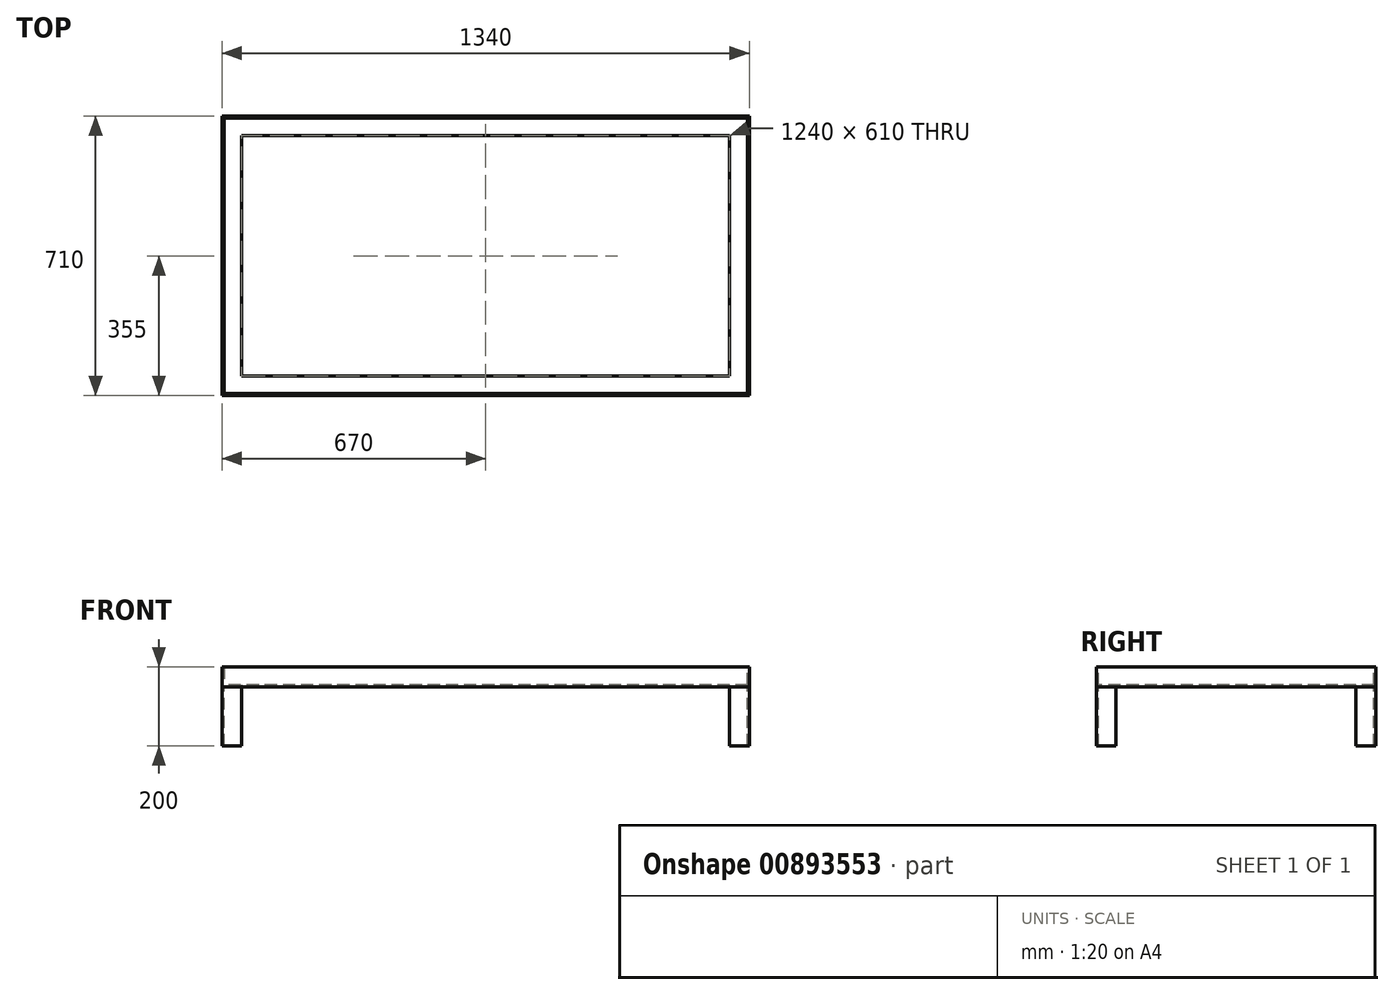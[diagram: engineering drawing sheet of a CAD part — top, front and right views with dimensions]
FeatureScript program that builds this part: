
annotation { "Feature Type Name" : "Feature", "Feature Type Description" : "" }
export const myFeature = defineFeature(function(context is Context, id is Id, definition is map)
    precondition{}
    {
        {
            var Q0;
            Q0=qCreatedBy(makeId("Right.planeOp"),FACE);
            var sketch = newSketch(context, id + "F0", { "sketchPlane" : qUnion([Q0])});
            skLineSegment(sketch, "E0.bottom", {"start": v(0, 0) * mm, "end": v(-50, 0) * mm});
            skLineSegment(sketch, "E0.top", {"start": v(-5, 5) * mm, "end": v(-50, 5) * mm});
            skLineSegment(sketch, "E0.left", {"start": v(0, 0) * mm, "end": v(0, 5) * mm});
            skLineSegment(sketch, "E0.right", {"start": v(-50, 0) * mm, "end": v(-50, 5) * mm});
            skLineSegment(sketch, "E1.bottom", {"start": v(0, 0) * mm, "end": v(-5, 0) * mm});
            skLineSegment(sketch, "E1.top", {"start": v(0, 50) * mm, "end": v(-5, 50) * mm});
            skLineSegment(sketch, "E1.left", {"start": v(0, 0) * mm, "end": v(0, 50) * mm});
            skLineSegment(sketch, "E1.right", {"start": v(-5, 5) * mm, "end": v(-5, 50) * mm});
            skSolve(sketch);
        }
        {
            var Q0;
            Q0 = qSketchRegion(id + "F0", true);
            extrude(context, id + "F1", {"entities" : qUnion([Q0]), "endBound" : BoundingType.SYMMETRIC, "depth" : 1340 * mm, "offsetDistance" : 25 * mm});
        }
        {
            var Q0;
            Q0=makeQuery(id+"F1.opExtrude","SWEPT_FACE",FACE,{"disambiguationData":[OSD([sQuery(id+"F0.wireOp",EDGE,"E1.left")])]});
            var sketch = newSketch(context, id + "F2", { "sketchPlane" : qUnion([Q0])});
            skLineSegment(sketch, "E2", {"start": v(670, 0) * mm, "end": v(620, 0) * mm});
            skLineSegment(sketch, "E3", {"start": v(620, 0) * mm, "end": v(620, 5) * mm});
            skLineSegment(sketch, "E4", {"start": v(620, 5) * mm, "end": v(665, 5) * mm});
            skLineSegment(sketch, "E5", {"start": v(665, 5) * mm, "end": v(665, 50) * mm});
            skLineSegment(sketch, "E6", {"start": v(665, 50) * mm, "end": v(670, 50) * mm});
            skLineSegment(sketch, "E7", {"start": v(670, 50) * mm, "end": v(670, 0) * mm});
            skSolve(sketch);
        }
        {
            var Q0;
            Q0 = qSketchRegion(id + "F2", true);
            extrude(context, id + "F3", {"entities" : qUnion([Q0]), "operationType" : NewBodyOperationType.ADD, "oppositeDirection" : true, "depth" : 710 * mm, "offsetDistance" : 25 * mm});
        }
        {
            var Q0;
            Q0=makeQuery(id+"F3.boolean.opBoolean","MERGE",FACE,{"derivedFrom":[makeQuery(id+"F1.opExtrude","CAP_FACE",FACE,{"disambiguationData":[OSD([sQuery(id+"F0.wireOp",EDGE,"E0.bottom"),sQuery(id+"F0.wireOp",EDGE,"E0.top"),sQuery(id+"F0.wireOp",EDGE,"E0.right"),sQuery(id+"F0.wireOp",EDGE,"E1.bottom"),sQuery(id+"F0.wireOp",EDGE,"E1.top"),sQuery(id+"F0.wireOp",EDGE,"E1.left"),sQuery(id+"F0.wireOp",EDGE,"E1.right")])],"isStart":true}),makeQuery(id+"F3.opExtrude","SWEPT_FACE",FACE,{"disambiguationData":[OSD([sQuery(id+"F2.wireOp",EDGE,"E7")])]})]});
            var sketch = newSketch(context, id + "F4", { "sketchPlane" : qUnion([Q0])});
            skLineSegment(sketch, "E8", {"start": v(710, 50) * mm, "end": v(710, 0) * mm});
            skLineSegment(sketch, "E9", {"start": v(710, 0) * mm, "end": v(660, 0) * mm});
            skLineSegment(sketch, "E10", {"start": v(660, 0) * mm, "end": v(660, 5) * mm});
            skLineSegment(sketch, "E11", {"start": v(660, 5) * mm, "end": v(705, 5) * mm});
            skLineSegment(sketch, "E12", {"start": v(705, 5) * mm, "end": v(705, 50) * mm});
            skLineSegment(sketch, "E13", {"start": v(705, 50) * mm, "end": v(710, 50) * mm});
            skSolve(sketch);
        }
        {
            var Q0;
            Q0 = qSketchRegion(id + "F4", true);
            extrude(context, id + "F5", {"entities" : qUnion([Q0]), "operationType" : NewBodyOperationType.ADD, "oppositeDirection" : true, "depth" : 1340 * mm, "offsetDistance" : 25 * mm});
        }
        {
            var Q0;
            Q0=makeQuery(id+"F5.boolean.opBoolean","MERGE",FACE,{"derivedFrom":[makeQuery(id+"F3.opExtrude","CAP_FACE",FACE,{"disambiguationData":[OSD([sQuery(id+"F2.wireOp",EDGE,"E2"),sQuery(id+"F2.wireOp",EDGE,"E3"),sQuery(id+"F2.wireOp",EDGE,"E4"),sQuery(id+"F2.wireOp",EDGE,"E5"),sQuery(id+"F2.wireOp",EDGE,"E6"),sQuery(id+"F2.wireOp",EDGE,"E7")])],"isStart":false}),makeQuery(id+"F5.opExtrude","SWEPT_FACE",FACE,{"disambiguationData":[OSD([sQuery(id+"F4.wireOp",EDGE,"E8")])]})]});
            var sketch = newSketch(context, id + "F6", { "sketchPlane" : qUnion([Q0])});
            skLineSegment(sketch, "E14", {"start": v(670, 50) * mm, "end": v(670, 0) * mm});
            skLineSegment(sketch, "E15", {"start": v(670, 0) * mm, "end": v(620, 0) * mm});
            skLineSegment(sketch, "E16", {"start": v(620, 0) * mm, "end": v(620, 5) * mm});
            skLineSegment(sketch, "E17", {"start": v(620, 5) * mm, "end": v(665, 5) * mm});
            skLineSegment(sketch, "E18", {"start": v(665, 5) * mm, "end": v(665, 50) * mm});
            skLineSegment(sketch, "E19", {"start": v(665, 50) * mm, "end": v(670, 50) * mm});
            skSolve(sketch);
        }
        {
            var Q0;
            Q0 = qSketchRegion(id + "F6", true);
            extrude(context, id + "F7", {"entities" : qUnion([Q0]), "operationType" : NewBodyOperationType.ADD, "oppositeDirection" : true, "depth" : 710 * mm, "offsetDistance" : 25 * mm});
        }
        {
            var Q0;
            Q0=makeQuery(id+"F7.boolean.opBoolean","MERGE",FACE,{"derivedFrom":[makeQuery(id+"F5.boolean.opBoolean","MERGE",FACE,{"derivedFrom":[makeQuery(id+"F3.boolean.opBoolean","MERGE",FACE,{"derivedFrom":[makeQuery(id+"F1.opExtrude","SWEPT_FACE",FACE,{"disambiguationData":[OSD([sQuery(id+"F0.wireOp",EDGE,"E0.bottom"),sQuery(id+"F0.wireOp",EDGE,"E1.bottom")])]}),makeQuery(id+"F3.opExtrude","SWEPT_FACE",FACE,{"disambiguationData":[OSD([sQuery(id+"F2.wireOp",EDGE,"E2")])]})]}),makeQuery(id+"F5.opExtrude","SWEPT_FACE",FACE,{"disambiguationData":[OSD([sQuery(id+"F4.wireOp",EDGE,"E9")])]})]}),makeQuery(id+"F7.opExtrude","SWEPT_FACE",FACE,{"disambiguationData":[OSD([sQuery(id+"F6.wireOp",EDGE,"E15")])]})]});
            var sketch = newSketch(context, id + "F8", { "sketchPlane" : qUnion([Q0])});
            skLineSegment(sketch, "E20", {"start": v(-670, 0) * mm, "end": v(-670, 50) * mm});
            skLineSegment(sketch, "E21", {"start": v(-670, 50) * mm, "end": v(-665, 50) * mm});
            skLineSegment(sketch, "E22", {"start": v(-665, 50) * mm, "end": v(-665, 5) * mm});
            skLineSegment(sketch, "E23", {"start": v(-665, 5) * mm, "end": v(-620, 5) * mm});
            skLineSegment(sketch, "E24", {"start": v(-620, 5) * mm, "end": v(-620, 0) * mm});
            skLineSegment(sketch, "E25", {"start": v(-620, 0) * mm, "end": v(-670, 0) * mm});
            skLineSegment(sketch, "E26", {"start": v(-670, 710) * mm, "end": v(-670, 660) * mm});
            skLineSegment(sketch, "E27", {"start": v(-670, 660) * mm, "end": v(-665, 660) * mm});
            skLineSegment(sketch, "E28", {"start": v(-665, 660) * mm, "end": v(-665, 705) * mm});
            skLineSegment(sketch, "E29", {"start": v(-665, 705) * mm, "end": v(-620, 705) * mm});
            skLineSegment(sketch, "E30", {"start": v(-620, 705) * mm, "end": v(-620, 710) * mm});
            skLineSegment(sketch, "E31", {"start": v(-620, 710) * mm, "end": v(-670, 710) * mm});
            skLineSegment(sketch, "E32.MirrorCS", {"start": v(620, 0) * mm, "end": v(670, 0) * mm});
            skLineSegment(sketch, "E33.MirrorCS", {"start": v(665, 5) * mm, "end": v(620, 5) * mm});
            skLineSegment(sketch, "E34.MirrorCS", {"start": v(620, 5) * mm, "end": v(620, 0) * mm});
            skLineSegment(sketch, "E35.MirrorCS", {"start": v(670, 50) * mm, "end": v(665, 50) * mm});
            skLineSegment(sketch, "E36.MirrorCS", {"start": v(665, 50) * mm, "end": v(665, 5) * mm});
            skLineSegment(sketch, "E37.MirrorCS", {"start": v(670, 0) * mm, "end": v(670, 50) * mm});
            skLineSegment(sketch, "E38.MirrorCS", {"start": v(620, 705) * mm, "end": v(620, 710) * mm});
            skLineSegment(sketch, "E39.MirrorCS", {"start": v(620, 710) * mm, "end": v(670, 710) * mm});
            skLineSegment(sketch, "E40.MirrorCS", {"start": v(670, 660) * mm, "end": v(665, 660) * mm});
            skLineSegment(sketch, "E41.MirrorCS", {"start": v(670, 710) * mm, "end": v(670, 660) * mm});
            skLineSegment(sketch, "E42.MirrorCS", {"start": v(665, 705) * mm, "end": v(620, 705) * mm});
            skLineSegment(sketch, "E43.MirrorCS", {"start": v(665, 660) * mm, "end": v(665, 705) * mm});
            skSolve(sketch);
        }
        {
            var Q0;
            Q0 = qSketchRegion(id + "F8", true);
            extrude(context, id + "F9", {"entities" : qUnion([Q0]), "depth" : 150 * mm, "offsetDistance" : 25 * mm});
        }
    });
